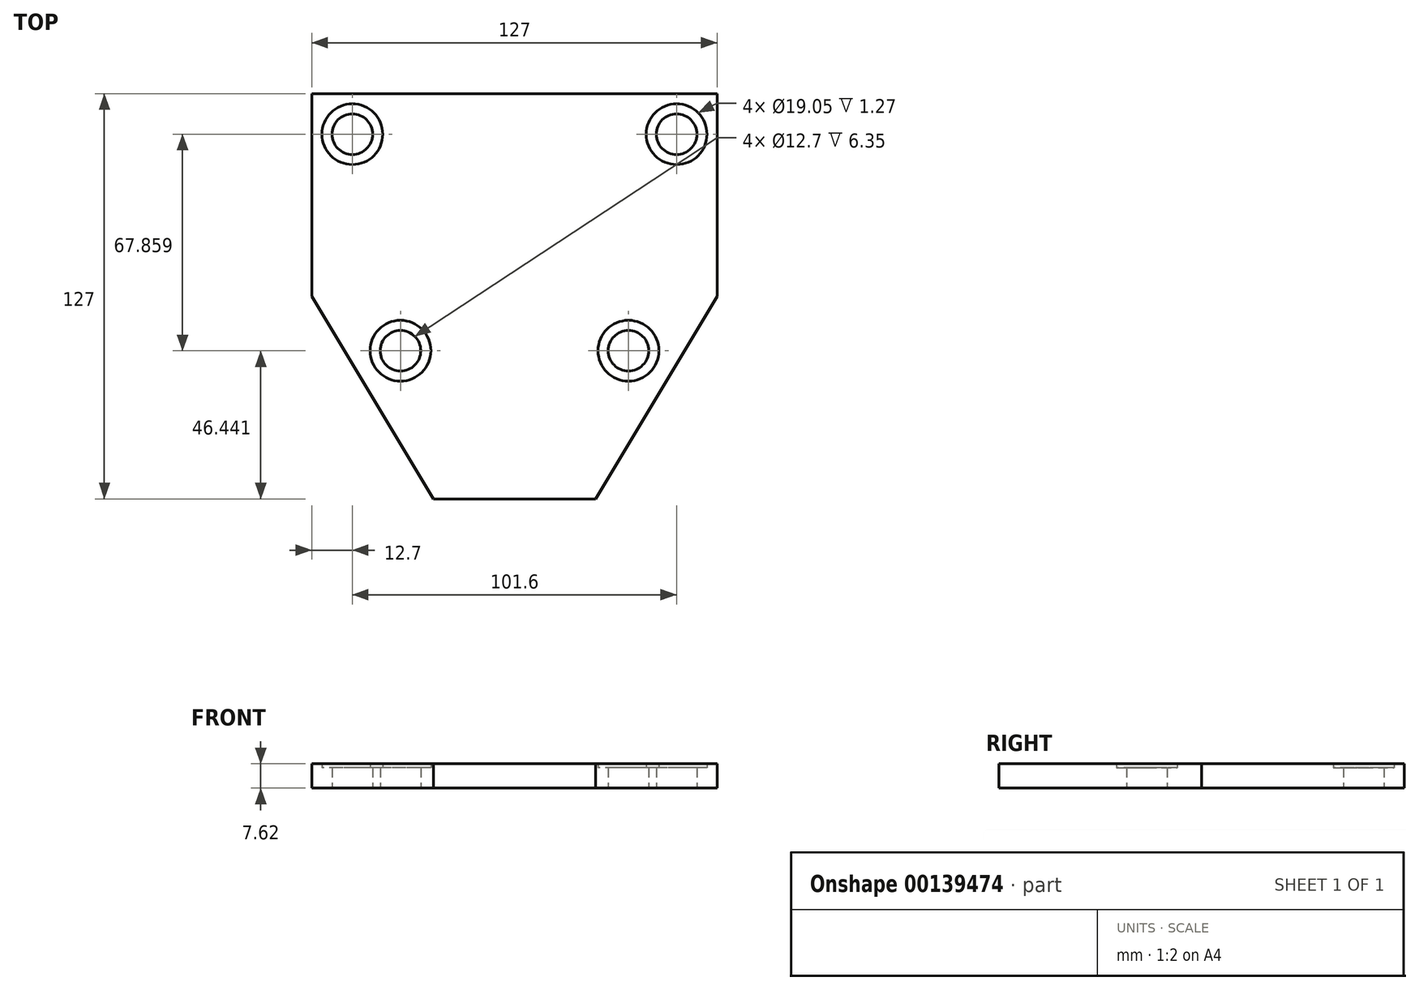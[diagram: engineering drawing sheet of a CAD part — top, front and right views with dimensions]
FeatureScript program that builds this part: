
annotation { "Feature Type Name" : "Feature", "Feature Type Description" : "" }
export const myFeature = defineFeature(function(context is Context, id is Id, definition is map)
    precondition{}
    {
        {
            var Q0;
            Q0=qCreatedBy(makeId("Top.planeOp"),FACE);
            var sketch = newSketch(context, id + "F0", { "sketchPlane" : qUnion([Q0])});
            skLineSegment(sketch, "E0", {"start": v(-25.4, -63.5) * mm, "end": v(25.4, -63.5) * mm});
            skLineSegment(sketch, "E1", {"start": v(25.4, -63.5) * mm, "end": v(63.5, 0) * mm});
            skLineSegment(sketch, "E2", {"start": v(63.5, 0) * mm, "end": v(63.5, 63.5) * mm});
            skLineSegment(sketch, "E3", {"start": v(63.5, 63.5) * mm, "end": v(-63.5, 63.5) * mm});
            skLineSegment(sketch, "E4", {"start": v(-63.5, 63.5) * mm, "end": v(-63.5, 0) * mm});
            skLineSegment(sketch, "E5", {"start": v(-63.5, 0) * mm, "end": v(-25.4, -63.5) * mm});
            skCircle(sketch, "E6", {"center": v(-50.8, 50.8) * mm, "radius": 6.35 * mm});
            skCircle(sketch, "E7", {"center": v(50.8, 50.8) * mm, "radius": 6.35 * mm});
            skCircle(sketch, "E8", {"center": v(35.72, -17.06) * mm, "radius": 6.35 * mm});
            skCircle(sketch, "E9", {"center": v(-35.72, -17.06) * mm, "radius": 6.35 * mm});
            skCircle(sketch, "E10", {"center": v(-50.8, 50.8) * mm, "radius": 9.53 * mm});
            skCircle(sketch, "E11", {"center": v(-35.72, -17.06) * mm, "radius": 9.53 * mm});
            skCircle(sketch, "E12", {"center": v(35.72, -17.06) * mm, "radius": 9.53 * mm});
            skCircle(sketch, "E13", {"center": v(50.8, 50.8) * mm, "radius": 9.53 * mm});
            skLineSegment(sketch, "E14", {"start": v(0, 63.5) * mm, "end": v(0, -63.5) * mm, "construction": true});
            skLineSegment(sketch, "E15", {"start": v(63.5, 0) * mm, "end": v(-63.5, 0) * mm, "construction": true});
            skPoint(sketch, "E16", {"position": v(0, 0) * mm});
            skSolve(sketch);
        }
        {
            var Q0;
            Q0=qCreatedBy(makeId("Top.planeOp"),FACE);
            var sketch = newSketch(context, id + "F1", { "sketchPlane" : qUnion([Q0])});
            skSolve(sketch);
        }
        {
            var Q0;
            Q0 = qSketchRegion(id + "F1", true);
            var Q1;
            Q1=makeQuery(id+"F0.imprint","IMPRINT",FACE,{"disambiguationData":[TD([[makeQuery(id+"F0.imprint","IMPRINT",EDGE,{"derivedFrom":sQuery(id+"F0.wireOp",EDGE,"E0")}),1.0]])]});
            extrude(context, id + "F2", {"entities" : qUnion([Q0, Q1]), "depth" : 7.62 * mm});
        }
        {
            var Q0;
            Q0=makeQuery(id+"F0.imprint","IMPRINT",FACE,{"disambiguationData":[TD([[makeQuery(id+"F0.imprint","IMPRINT",EDGE,{"derivedFrom":sQuery(id+"F0.wireOp",EDGE,"E6")}),-1.0]])]});
            var Q1;
            Q1=makeQuery(id+"F0.imprint","IMPRINT",FACE,{"disambiguationData":[TD([[makeQuery(id+"F0.imprint","IMPRINT",EDGE,{"derivedFrom":sQuery(id+"F0.wireOp",EDGE,"E7")}),-1.0]])]});
            var Q2;
            Q2=makeQuery(id+"F0.imprint","IMPRINT",FACE,{"disambiguationData":[TD([[makeQuery(id+"F0.imprint","IMPRINT",EDGE,{"derivedFrom":sQuery(id+"F0.wireOp",EDGE,"E8")}),-1.0]])]});
            var Q3;
            Q3=makeQuery(id+"F0.imprint","IMPRINT",FACE,{"disambiguationData":[TD([[makeQuery(id+"F0.imprint","IMPRINT",EDGE,{"derivedFrom":sQuery(id+"F0.wireOp",EDGE,"E9")}),-1.0]])]});
            extrude(context, id + "F3", {"entities" : qUnion([Q0, Q1, Q2, Q3]), "operationType" : NewBodyOperationType.ADD, "depth" : 6.35 * mm});
        }
    });
